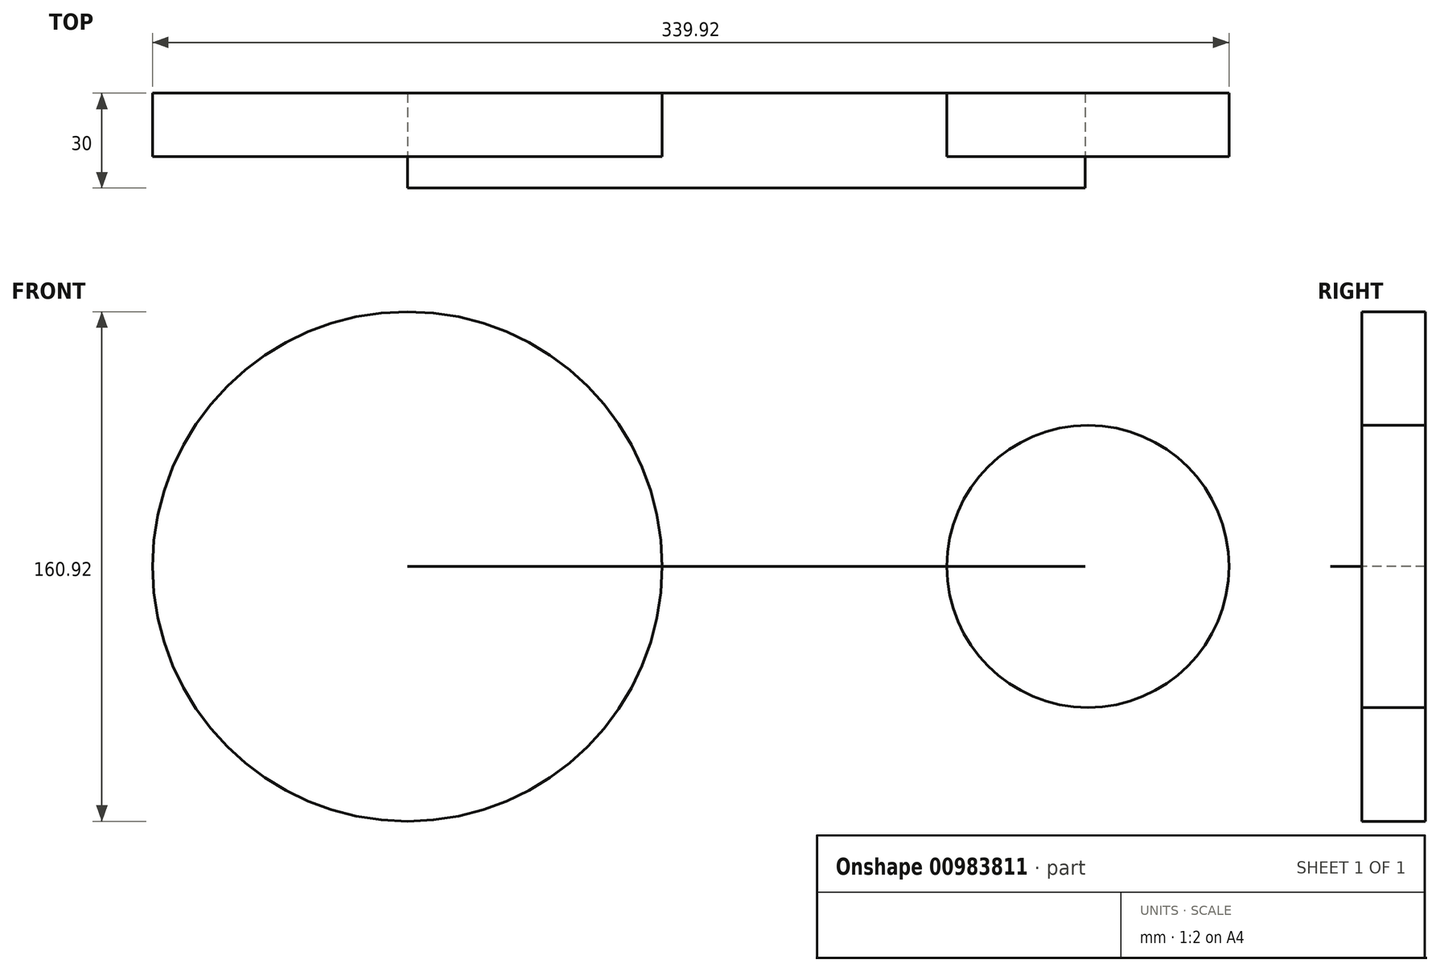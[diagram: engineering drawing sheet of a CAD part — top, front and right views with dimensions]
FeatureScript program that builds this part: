
annotation { "Feature Type Name" : "Feature", "Feature Type Description" : "" }
export const myFeature = defineFeature(function(context is Context, id is Id, definition is map)
    precondition{}
    {
        {
            var Q0;
            Q0=qCreatedBy(makeId("Front.planeOp"),FACE);
            var sketch = newSketch(context, id + "F0", { "sketchPlane" : qUnion([Q0])});
            skCircle(sketch, "E0", {"center": v(0, 0) * mm, "radius": 80.46 * mm});
            skSolve(sketch);
        }
        {
            var Q0;
            Q0=qCreatedBy(makeId("Front.planeOp"),FACE);
            var sketch = newSketch(context, id + "F1", { "sketchPlane" : qUnion([Q0])});
            skCircle(sketch, "E1", {"center": v(214.91, 0) * mm, "radius": 44.54 * mm});
            skSolve(sketch);
        }
        {
            var Q0;
            Q0=qCreatedBy(makeId("Front.planeOp"),FACE);
            var sketch = newSketch(context, id + "F2", { "sketchPlane" : qUnion([Q0])});
            skLineSegment(sketch, "E2", {"start": v(0, 0) * mm, "end": v(214.08, 0) * mm});
            skSolve(sketch);
        }
        {
            var Q0;
            Q0=sQuery(id+"F0.wireOp",EDGE,"E0");
            extrude(context, id + "F3", {"bodyType" : ToolBodyType.SURFACE, "surfaceEntities" : qUnion([Q0]), "depth" : 20 * mm, "offsetDistance" : 25 * mm});
        }
        {
            var Q0;
            Q0=sQuery(id+"F2.wireOp",EDGE,"E2");
            extrude(context, id + "F4", {"bodyType" : ToolBodyType.SURFACE, "surfaceEntities" : qUnion([Q0]), "depth" : 30 * mm, "offsetDistance" : 25 * mm});
        }
        {
            var Q0;
            Q0=sQuery(id+"F1.wireOp",EDGE,"E1");
            extrude(context, id + "F5", {"bodyType" : ToolBodyType.SURFACE, "surfaceEntities" : qUnion([Q0]), "depth" : 20 * mm, "offsetDistance" : 25 * mm});
        }
    });
